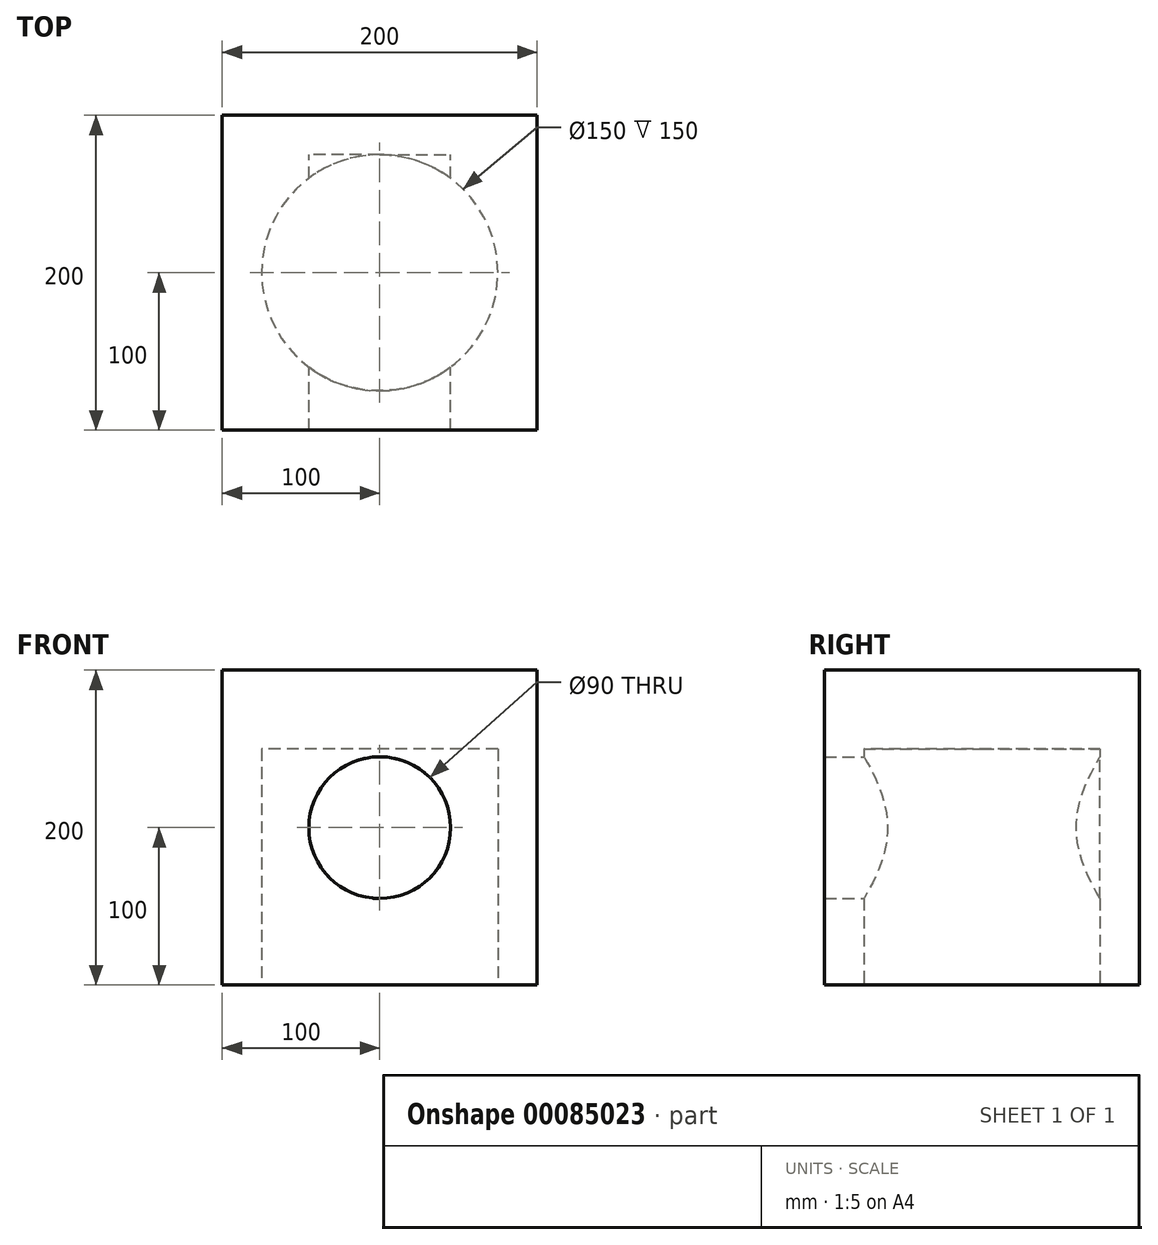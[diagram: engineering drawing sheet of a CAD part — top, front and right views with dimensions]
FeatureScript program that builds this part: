
annotation { "Feature Type Name" : "Feature", "Feature Type Description" : "" }
export const myFeature = defineFeature(function(context is Context, id is Id, definition is map)
    precondition{}
    {
        {
            var Q0;
            Q0=qCreatedBy(makeId("Front.planeOp"),FACE);
            var sketch = newSketch(context, id + "F0", { "sketchPlane" : qUnion([Q0])});
            skLineSegment(sketch, "E0", {"start": v(0, 0) * mm, "end": v(0, 200) * mm});
            skLineSegment(sketch, "E1", {"start": v(0, 200) * mm, "end": v(200, 200) * mm});
            skLineSegment(sketch, "E2", {"start": v(200, 200) * mm, "end": v(200, 0) * mm});
            skLineSegment(sketch, "E3", {"start": v(200, 0) * mm, "end": v(0, 0) * mm});
            skCircle(sketch, "E4", {"center": v(100, 100) * mm, "radius": 45 * mm});
            skLineSegment(sketch, "E5", {"start": v(100, 100) * mm, "end": v(100, 145) * mm});
            skSolve(sketch);
        }
        {
            var Q0;
            Q0 = qSketchRegion(id + "F0", true);
            extrude(context, id + "F1", {"entities" : qUnion([Q0]), "depth" : 200 * mm});
        }
        {
            var Q0;
            Q0=qCreatedBy(makeId("Top.planeOp"),FACE);
            var sketch = newSketch(context, id + "F2", { "sketchPlane" : qUnion([Q0])});
            skLineSegment(sketch, "E6.bottom", {"start": v(0, 0) * mm, "end": v(200, 0) * mm});
            skLineSegment(sketch, "E6.top", {"start": v(0, -200) * mm, "end": v(200, -200) * mm});
            skLineSegment(sketch, "E6.left", {"start": v(0, 0) * mm, "end": v(0, -200) * mm});
            skLineSegment(sketch, "E6.right", {"start": v(200, 0) * mm, "end": v(200, -200) * mm});
            skCircle(sketch, "E7", {"center": v(100, -100) * mm, "radius": 75 * mm});
            skLineSegment(sketch, "E8", {"start": v(100, -100) * mm, "end": v(100, -175) * mm});
            skSolve(sketch);
        }
        {
            var Q0;
            Q0=makeQuery(id+"F2.imprint","IMPRINT",FACE,{"disambiguationData":[TD([[makeQuery(id+"F2.imprint","IMPRINT",EDGE,{"derivedFrom":sQuery(id+"F2.wireOp",EDGE,"E7")}),1.0]])]});
            extrude(context, id + "F3", {"entities" : qUnion([Q0]), "operationType" : NewBodyOperationType.REMOVE, "depth" : 150 * mm});
        }
        {
            var Q0;
            Q0=makeQuery(id+"F0.imprint","IMPRINT",FACE,{"disambiguationData":[TD([[makeQuery(id+"F0.imprint","IMPRINT",EDGE,{"derivedFrom":sQuery(id+"F0.wireOp",EDGE,"E4")}),1.0]])]});
            var Q1;
            Q1=makeQuery(id+"F1.opExtrude","SWEPT_FACE",FACE,{"disambiguationData":[OSD([sQuery(id+"F0.wireOp",EDGE,"E4")])]});
            var Q2;
            Q2=makeQuery(id+"F1.opExtrude","SWEPT_BODY",BODY,{"disambiguationData":[OSD([sQuery(id+"F0.wireOp",EDGE,"E0"),sQuery(id+"F0.wireOp",EDGE,"E1"),sQuery(id+"F0.wireOp",EDGE,"E2"),sQuery(id+"F0.wireOp",EDGE,"E3"),sQuery(id+"F0.wireOp",EDGE,"E4")])]});
            extrude(context, id + "F4", {"entities" : qUnion([Q0]), "operationType" : NewBodyOperationType.ADD, "endBoundEntityFace" : qUnion([Q1]), "endBoundEntityBody" : qUnion([Q2]), "depth" : 25 * mm});
        }
    });
